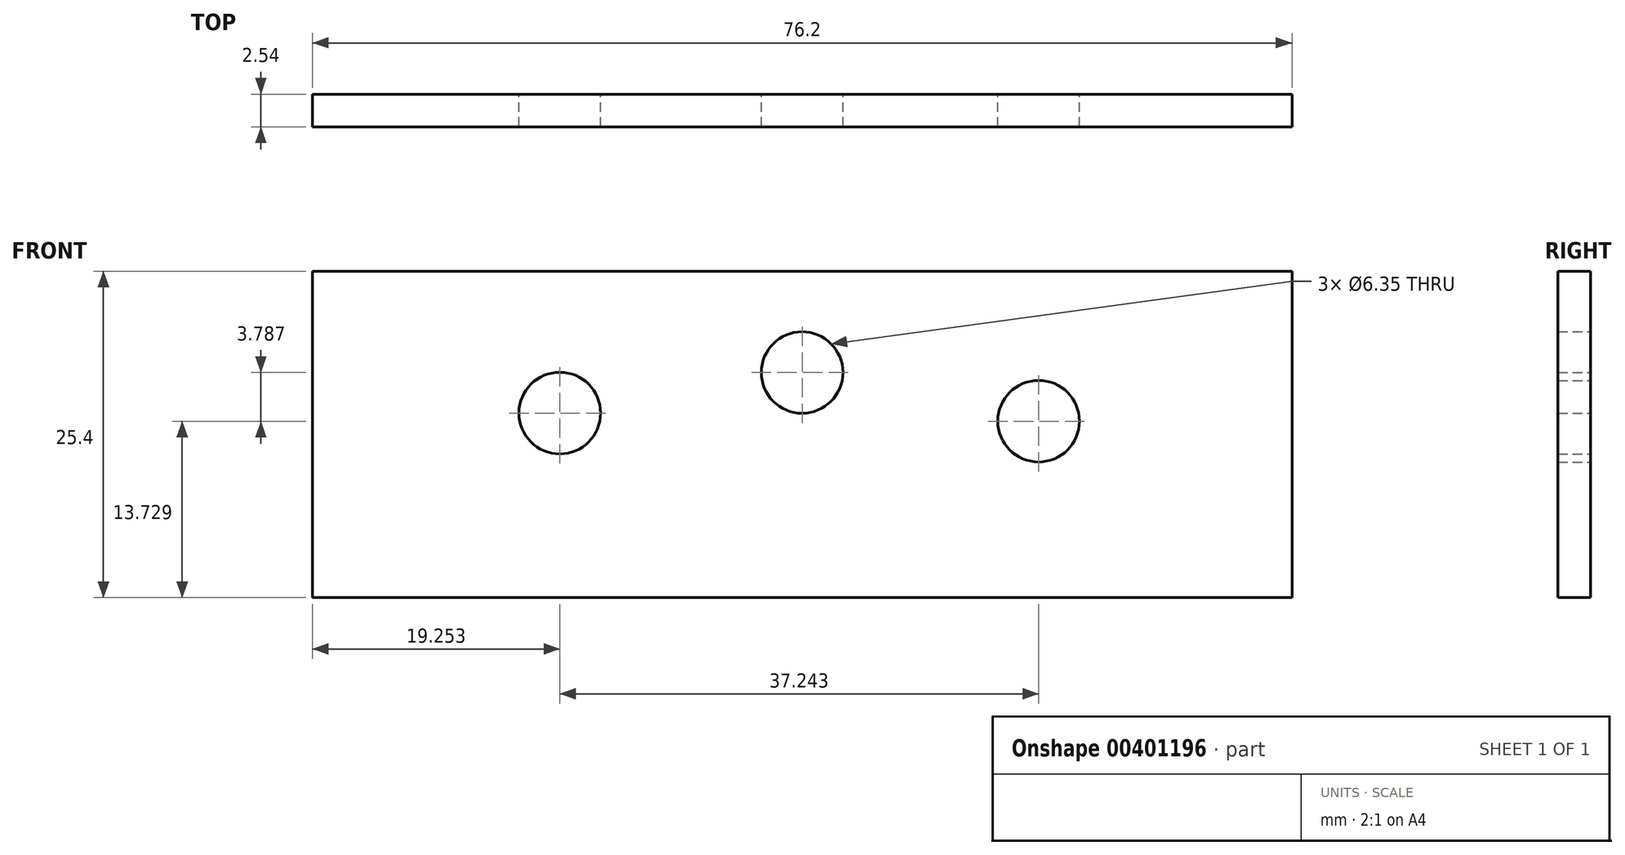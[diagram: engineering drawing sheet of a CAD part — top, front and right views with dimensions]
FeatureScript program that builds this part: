
annotation { "Feature Type Name" : "Feature", "Feature Type Description" : "" }
export const myFeature = defineFeature(function(context is Context, id is Id, definition is map)
    precondition{}
    {
        {
            var Q0;
            Q0=qCreatedBy(makeId("Front.planeOp"),FACE);
            var sketch = newSketch(context, id + "F0", { "sketchPlane" : qUnion([Q0])});
            skLineSegment(sketch, "E0.bottom", {"start": v(0, 0) * mm, "end": v(76.2, 0) * mm});
            skLineSegment(sketch, "E0.top", {"start": v(0, 25.4) * mm, "end": v(76.2, 25.4) * mm});
            skLineSegment(sketch, "E0.left", {"start": v(0, 0) * mm, "end": v(0, 25.4) * mm});
            skLineSegment(sketch, "E0.right", {"start": v(76.2, 0) * mm, "end": v(76.2, 25.4) * mm});
            skCircle(sketch, "E1", {"center": v(38.1, 17.52) * mm, "radius": 3.18 * mm});
            skPoint(sketch, "E1.centerSnap0", {"position": v(38.1, 25.4) * mm});
            skCircle(sketch, "E2", {"center": v(56.5, 13.73) * mm, "radius": 3.18 * mm});
            skCircle(sketch, "E3", {"center": v(19.25, 14.36) * mm, "radius": 3.18 * mm});
            skSolve(sketch);
        }
        {
            var Q0;
            Q0 = qSketchRegion(id + "F0", true);
            extrude(context, id + "F1", {"entities" : qUnion([Q0]), "depth" : 2.54 * mm});
        }
        {
            var Q0;
            Q0 = qSketchRegion(id + "F0", true);
            extrude(context, id + "F2", {"entities" : qUnion([Q0]), "operationType" : NewBodyOperationType.REMOVE, "oppositeDirection" : true, "depth" : 25.4 * mm});
        }
    });
